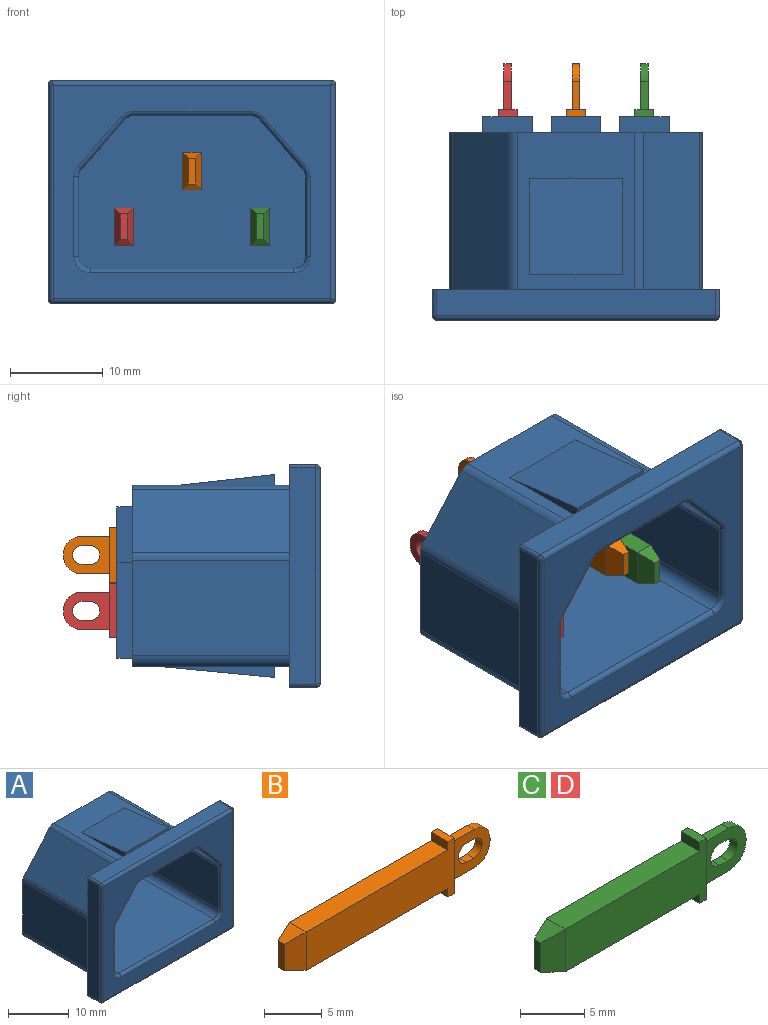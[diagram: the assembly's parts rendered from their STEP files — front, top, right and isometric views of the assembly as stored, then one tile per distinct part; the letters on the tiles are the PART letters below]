
ASSEMBLY  parts=4 mates=3
PART A: 98 faces, bbox 30.9x21.9x24.1 mm
  f0: plane 27.18x19.58mm, normal (0,1,0), area 315.8mm2, adj f45,f46,f47,f48,f49,f50,f52,f53
  f1: plane 12.05x1.14mm, normal (1,0,0), area 6.9mm2, adj f48,f62,f67
  f2: plane 10.31x1.14mm, normal (-1,0,0), area 5.9mm2, adj f45,f59,f60
  f3: plane 18.67x5.33mm, normal (0.75,0,-0.66), area 132.2mm2, adj f19,f24,f35,f51
  f4: plane 18.67x12.56mm, normal (0,0,-1), area 234.6mm2, adj f19,f20,f31,f51
  f5: plane 18.67x5.33mm, normal (-0.75,0,-0.66), area 132.2mm2, adj f20,f21,f27,f51
  f6: plane 18.67x8.57mm, normal (-1,0,0), area 159.9mm2, adj f21,f22,f26,f51
  f7: plane 21.89x18.67mm, normal (0,0,1), area 408.8mm2, adj f22,f23,f30,f51
  f8: plane 23.29x2.79mm, normal (-1,0,0), area 65.1mm2, adj f14,f15,f18,f42
  f9: plane 30.18x2.79mm, normal (0,0,-1), area 84.3mm2, adj f14,f15,f16,f43
  f10: plane 23.29x2.79mm, normal (1,0,0), area 65.1mm2, adj f14,f16,f17,f39
  f11: plane 30.18x2.79mm, normal (0,0,1), area 84.3mm2, adj f14,f17,f18,f38
  f12: plane 18.67x8.57mm, normal (1,0,0), area 159.9mm2, adj f23,f24,f34,f51
  f13: plane 29.92x23.04mm, normal (0,-1,0), area 283.1mm2, adj f25,f26,f27,f28,f29,f30,f31,f32
  f14: plane 30.94x24.05mm, normal (0,1,0), area 263.3mm2, adj f8,f9,f10,f11,f15,f16,f17,f18
  f15: cylinder r=0.38mm len=2.79mm, axis (0,-1,0), area 1.7mm2, adj f8,f9,f14,f44
  f16: cylinder r=0.38mm len=2.79mm, axis (0,1,0), area 1.7mm2, adj f9,f10,f14,f41
  f17: cylinder r=0.38mm len=2.79mm, axis (0,-1,0), area 1.7mm2, adj f10,f11,f14,f37
  f18: cylinder r=0.38mm len=2.79mm, axis (0,1,0), area 1.7mm2, adj f8,f11,f14,f40
  f19: cylinder r=1.27mm len=18.67mm, axis (0,-1,0), area 20.2mm2, adj f3,f4,f33,f51
  f20: cylinder r=1.27mm len=18.67mm, axis (0,-1,0), area 20.2mm2, adj f4,f5,f29,f51
  f21: cylinder r=1.27mm len=18.67mm, axis (0,-1,0), area 17.1mm2, adj f5,f6,f25,f51
  f22: cylinder r=1.27mm len=18.67mm, axis (0,-1,0), area 37.2mm2, adj f6,f7,f28,f51
  f23: cylinder r=1.27mm len=18.67mm, axis (0,-1,0), area 37.2mm2, adj f7,f12,f32,f51
  f24: cylinder r=1.27mm len=18.67mm, axis (0,-1,0), area 17.1mm2, adj f3,f12,f36,f51
  f25: torus R=1.78mm, axis (0,-1,0), area 0.8mm2, adj f13,f21,f26,f27
  f26: cylinder r=0.51mm len=8.57mm, axis (0,0,1), area 6.8mm2, adj f6,f13,f25,f28
  f27: cylinder r=0.51mm len=5.66mm, axis (-0.66,0,0.75), area 5.7mm2, adj f5,f13,f25,f29
  f28: torus R=1.78mm, axis (0,-1,0), area 1.8mm2, adj f13,f22,f26,f30
  f29: torus R=1.78mm, axis (0,-1,0), area 1mm2, adj f13,f20,f27,f31
  f30: cylinder r=0.51mm len=21.89mm, axis (1,0,0), area 17.5mm2, adj f7,f13,f28,f32
  f31: cylinder r=0.51mm len=12.56mm, axis (-1,0,0), area 10mm2, adj f4,f13,f29,f33
  f32: torus R=1.78mm, axis (0,-1,0), area 1.8mm2, adj f13,f23,f30,f34
  f33: torus R=1.78mm, axis (0,-1,0), area 1mm2, adj f13,f19,f31,f35
  f34: cylinder r=0.51mm len=8.57mm, axis (0,0,-1), area 6.8mm2, adj f12,f13,f32,f36
  f35: cylinder r=0.51mm len=5.66mm, axis (-0.66,0,-0.75), area 5.7mm2, adj f3,f13,f33,f36
  f36: torus R=1.78mm, axis (0,-1,0), area 0.8mm2, adj f13,f24,f34,f35
  f37: bspline ~0.62x0.51mm, area 0.3mm2, adj f17,f38,f39
  f38: cylinder r=0.51mm len=30.18mm, axis (1,0,0), area 24mm2, adj f11,f13,f37,f40
  f39: cylinder r=0.51mm len=23.29mm, axis (0,0,-1), area 18.5mm2, adj f10,f13,f37,f41
  f40: bspline ~0.62x0.51mm, area 0.3mm2, adj f18,f38,f42
  f41: bspline ~0.62x0.51mm, area 0.3mm2, adj f16,f39,f43
  f42: cylinder r=0.51mm len=23.29mm, axis (0,0,1), area 18.5mm2, adj f8,f13,f40,f44
  f43: cylinder r=0.51mm len=30.18mm, axis (-1,0,0), area 24mm2, adj f9,f13,f41,f44
  f44: bspline ~0.62x0.51mm, area 0.3mm2, adj f15,f42,f43
  f45: plane 16.97x12.71mm, normal (0,0,1), area 112.7mm2, adj f0,f2,f14,f52,f57,f58,f59,f60
  f46: plane 16.97x6.81mm, normal (0.75,0,0.66), area 153.6mm2, adj f0,f14,f52,f53
  f47: plane 16.97x10.23mm, normal (1,0,0), area 173.6mm2, adj f0,f14,f53,f54
  f48: plane 24.64x16.97mm, normal (0,0,-1), area 307.9mm2, adj f0,f1,f14,f54,f55,f61,f62,f63
  f49: plane 16.97x10.23mm, normal (-1,0,0), area 173.6mm2, adj f0,f14,f55,f56
  f50: plane 16.97x6.81mm, normal (-0.75,0,0.66), area 153.6mm2, adj f0,f14,f56,f57
  f51: plane 24.44x16.43mm, normal (0,-1,0), area 367.9mm2, adj f3,f4,f5,f6,f7,f12,f19,f20
  f52: cylinder r=1.27mm len=16.97mm, axis (0,-1,0), area 18.4mm2, adj f0,f14,f45,f46
  f53: cylinder r=1.27mm len=16.97mm, axis (0,-1,0), area 15.5mm2, adj f0,f14,f46,f47
  f54: cylinder r=1.27mm len=16.97mm, axis (0,-1,0), area 33.8mm2, adj f0,f14,f47,f48
  f55: cylinder r=1.27mm len=16.97mm, axis (0,-1,0), area 33.8mm2, adj f0,f14,f48,f49
  f56: cylinder r=1.27mm len=16.97mm, axis (0,-1,0), area 15.5mm2, adj f0,f14,f49,f50
  f57: cylinder r=1.27mm len=16.97mm, axis (0,-1,0), area 18.4mm2, adj f0,f14,f45,f50
  f58: plane 10.31x1.14mm, normal (1,0,0), area 5.9mm2, adj f45,f59,f60
  f59: plane 9.98x1.14mm, normal (0,-1,0), area 11.4mm2, adj f2,f45,f58,f60
  f60: plane 10.31x9.98mm, normal (0,0.11,0.99), area 103.6mm2, adj f2,f45,f58,f59
  f61: plane 12.05x1.14mm, normal (-1,0,0), area 6.9mm2, adj f48,f62,f67
  f62: plane 4.57x1.14mm, normal (0,-1,0), area 5.2mm2, adj f1,f48,f61,f67
  f63: plane 12.05x1.14mm, normal (1,0,0), area 6.9mm2, adj f48,f64,f66
  f64: plane 4.57x1.14mm, normal (0,-1,0), area 5.2mm2, adj f48,f63,f65,f66
  f65: plane 12.05x1.14mm, normal (-1,0,0), area 6.9mm2, adj f48,f64,f66
  f66: plane 12.05x4.57mm, normal (0,0.09,-1), area 55.3mm2, adj f48,f63,f64,f65
  f67: plane 12.05x4.57mm, normal (0,0.09,-1), area 55.3mm2, adj f1,f48,f61,f62
  f68: plane 2.03x1.65mm, normal (0,0,-1), area 3.4mm2, adj f69,f75,f76,f77
  f69: plane 4.01x1.65mm, normal (1,0,0), area 6.6mm2, adj f68,f70,f76,f77
  f70: plane 2.03x1.65mm, normal (0,0,1), area 3.4mm2, adj f69,f75,f76,f77
  f71: plane 10.31x1.65mm, normal (-1,0,0), area 17mm2, adj f0,f72,f74,f76
  f72: plane 5.33x1.65mm, normal (0,0,1), area 8.8mm2, adj f0,f71,f73,f76
  f73: plane 10.31x1.65mm, normal (1,0,0), area 17mm2, adj f0,f72,f74,f76
  f74: plane 5.33x1.65mm, normal (0,0,-1), area 8.8mm2, adj f0,f71,f73,f76
  f75: plane 4.01x1.65mm, normal (-1,0,0), area 6.6mm2, adj f68,f70,f76,f77
  f76: plane 10.31x5.33mm, normal (0,1,0), area 46.9mm2, adj f68,f69,f70,f71,f72,f73,f74,f75
  f77: plane 4.01x2.03mm, normal (0,1,0), area 8.2mm2, adj f68,f69,f70,f75
  f78: plane 2.03x1.65mm, normal (0,0,-1), area 3.4mm2, adj f79,f85,f86,f87
  f79: plane 4.01x1.65mm, normal (1,0,0), area 6.6mm2, adj f78,f80,f86,f87
  f80: plane 2.03x1.65mm, normal (0,0,1), area 3.4mm2, adj f79,f85,f86,f87
  f81: plane 10.31x1.65mm, normal (-1,0,0), area 17mm2, adj f0,f82,f84,f86
  f82: plane 5.33x1.65mm, normal (0,0,1), area 8.8mm2, adj f0,f81,f83,f86
  f83: plane 10.31x1.65mm, normal (1,0,0), area 17mm2, adj f0,f82,f84,f86
  f84: plane 5.33x1.65mm, normal (0,0,-1), area 8.8mm2, adj f0,f81,f83,f86
  f85: plane 4.01x1.65mm, normal (-1,0,0), area 6.6mm2, adj f78,f80,f86,f87
  f86: plane 10.31x5.33mm, normal (0,1,0), area 46.9mm2, adj f78,f79,f80,f81,f82,f83,f84,f85
  f87: plane 4.01x2.03mm, normal (0,1,0), area 8.2mm2, adj f78,f79,f80,f85
  f88: plane 2.03x1.65mm, normal (0,0,-1), area 3.4mm2, adj f89,f95,f96,f97
  f89: plane 4.01x1.65mm, normal (1,0,0), area 6.6mm2, adj f88,f90,f96,f97
  f90: plane 2.03x1.65mm, normal (0,0,1), area 3.4mm2, adj f89,f95,f96,f97
  f91: plane 10.31x1.65mm, normal (-1,0,0), area 17mm2, adj f0,f92,f94,f96
  f92: plane 5.33x1.65mm, normal (0,0,1), area 8.8mm2, adj f0,f91,f93,f96
  f93: plane 10.31x1.65mm, normal (1,0,0), area 17mm2, adj f0,f92,f94,f96
  f94: plane 5.33x1.65mm, normal (0,0,-1), area 8.8mm2, adj f0,f91,f93,f96
  f95: plane 4.01x1.65mm, normal (-1,0,0), area 6.6mm2, adj f88,f90,f96,f97
  f96: plane 10.31x5.33mm, normal (0,1,0), area 46.9mm2, adj f88,f89,f90,f91,f92,f93,f94,f95
  f97: plane 4.01x2.03mm, normal (0,1,0), area 8.2mm2, adj f88,f89,f90,f95
PART B: 25 faces, bbox 25.1x2x5.8 mm
  f0: plane 3.07x0.84mm, normal (0,0,-1), area 2.6mm2, adj f1,f10,f15,f16
  f1: cylinder r=1.91mm len=1.91mm, axis (0,1,0), area 2.5mm2, adj f0,f2,f15,f16
  f2: plane 0.84x0.25mm, normal (1,0,0), area 0.2mm2, adj f1,f3,f15,f16
  f3: cylinder r=1.91mm len=1.91mm, axis (0,1,0), area 2.5mm2, adj f2,f4,f15,f16
  f4: plane 3.07x0.84mm, normal (0,0,1), area 2.6mm2, adj f3,f10,f15,f16
  f5: plane 17.35x2.03mm, normal (0,0,1), area 35.3mm2, adj f12,f13,f14,f22
  f6: plane 2.79x0.76mm, normal (-1,0,0), area 2.1mm2, adj f21,f22,f23,f24
  f7: plane 17.35x2.03mm, normal (0,0,-1), area 35.3mm2, adj f8,f13,f14,f23
  f8: plane 2.03x0.89mm, normal (-1,0,0), area 1.8mm2, adj f7,f9,f13,f14
  f9: plane 2.03x0.76mm, normal (0,0,-1), area 1.5mm2, adj f8,f10,f13,f14
  f10: plane 5.84x2.03mm, normal (1,0,0), area 8.5mm2, adj f0,f4,f9,f11,f13,f14,f15,f16
  f11: plane 2.03x0.76mm, normal (0,0,1), area 1.5mm2, adj f10,f12,f13,f14
  f12: plane 2.03x0.89mm, normal (-1,0,0), area 1.8mm2, adj f5,f11,f13,f14
  f13: plane 18.11x5.84mm, normal (0,-1,0), area 75mm2, adj f5,f7,f8,f9,f10,f11,f12,f24
  f14: plane 18.11x5.84mm, normal (0,1,0), area 75mm2, adj f5,f7,f8,f9,f10,f11,f12,f21
  f15: plane 4.98x4.06mm, normal (0,1,0), area 13.6mm2, adj f0,f1,f2,f3,f4,f10,f17,f18
  f16: plane 4.98x4.06mm, normal (0,-1,0), area 13.6mm2, adj f0,f1,f2,f3,f4,f10,f17,f18
  f17: plane 0.89x0.84mm, normal (0,0,1), area 0.7mm2, adj f15,f16,f18,f20
  f18: cylinder r=1.02mm len=2.03mm, axis (0,1,0), area 2.7mm2, adj f15,f16,f17,f19
  f19: plane 0.89x0.84mm, normal (0,0,-1), area 0.7mm2, adj f15,f16,f18,f20
  f20: cylinder r=1.02mm len=2.03mm, axis (0,1,0), area 2.7mm2, adj f15,f16,f17,f19
  f21: plane 4.06x2.03mm, normal (-0.3,0.95,0), area 7.3mm2, adj f6,f14,f22,f23
  f22: plane 2.03x2.03mm, normal (-0.3,0,0.95), area 3mm2, adj f5,f6,f21,f24
  f23: plane 2.03x2.03mm, normal (-0.3,0,-0.95), area 3mm2, adj f6,f7,f21,f24
  f24: plane 4.06x2.03mm, normal (-0.3,-0.95,0), area 7.3mm2, adj f6,f13,f22,f23
PART C: 25 faces, bbox 22.6x2x5.8 mm
  f0: plane 3.07x0.81mm, normal (0,0,-1), area 2.5mm2, adj f1,f10,f15,f16
  f1: cylinder r=1.91mm len=1.91mm, axis (0,1,0), area 2.4mm2, adj f0,f2,f15,f16
  f2: plane 0.81x0.25mm, normal (1,0,0), area 0.2mm2, adj f1,f3,f15,f16
  f3: cylinder r=1.91mm len=1.91mm, axis (0,1,0), area 2.4mm2, adj f2,f4,f15,f16
  f4: plane 3.07x0.81mm, normal (0,0,1), area 2.5mm2, adj f3,f10,f15,f16
  f5: plane 14.81x2.03mm, normal (0,0,1), area 30.1mm2, adj f12,f13,f14,f22
  f6: plane 2.79x0.76mm, normal (-1,0,0), area 2.1mm2, adj f21,f22,f23,f24
  f7: plane 14.81x2.03mm, normal (0,0,-1), area 30.1mm2, adj f8,f13,f14,f23
  f8: plane 2.03x0.89mm, normal (-1,0,0), area 1.8mm2, adj f7,f9,f13,f14
  f9: plane 2.03x0.76mm, normal (0,0,-1), area 1.5mm2, adj f8,f10,f13,f14
  f10: plane 5.84x2.03mm, normal (1,0,0), area 8.6mm2, adj f0,f4,f9,f11,f13,f14,f15,f16
  f11: plane 2.03x0.76mm, normal (0,0,1), area 1.5mm2, adj f10,f12,f13,f14
  f12: plane 2.03x0.89mm, normal (-1,0,0), area 1.8mm2, adj f5,f11,f13,f14
  f13: plane 15.57x5.84mm, normal (0,-1,0), area 64.6mm2, adj f5,f7,f8,f9,f10,f11,f12,f24
  f14: plane 15.57x5.84mm, normal (0,1,0), area 64.6mm2, adj f5,f7,f8,f9,f10,f11,f12,f21
  f15: plane 4.98x4.06mm, normal (0,1,0), area 13.6mm2, adj f0,f1,f2,f3,f4,f10,f17,f18
  f16: plane 4.98x4.06mm, normal (0,-1,0), area 13.6mm2, adj f0,f1,f2,f3,f4,f10,f17,f18
  f17: plane 0.89x0.81mm, normal (0,0,1), area 0.7mm2, adj f15,f16,f18,f20
  f18: cylinder r=1.02mm len=2.03mm, axis (0,1,0), area 2.6mm2, adj f15,f16,f17,f19
  f19: plane 0.89x0.81mm, normal (0,0,-1), area 0.7mm2, adj f15,f16,f18,f20
  f20: cylinder r=1.02mm len=2.03mm, axis (0,1,0), area 2.6mm2, adj f15,f16,f17,f19
  f21: plane 4.06x2.03mm, normal (-0.3,0.95,0), area 7.3mm2, adj f6,f14,f22,f23
  f22: plane 2.03x2.03mm, normal (-0.3,0,0.95), area 3mm2, adj f5,f6,f21,f24
  f23: plane 2.03x2.03mm, normal (-0.3,0,-0.95), area 3mm2, adj f6,f7,f21,f24
  f24: plane 4.06x2.03mm, normal (-0.3,-0.95,0), area 7.3mm2, adj f6,f13,f22,f23
PART D: same geometry as C
PLACE A t=(6.41,-4.91,18.4)mm
PLACE B rot(axis=(0,0,1),90deg) t=(-29.58,-11.35,31.74)mm
PLACE C rot(axis=(0,0,1),90deg) t=(-22.21,-5.27,3.32)mm
PLACE D rot(axis=(0,0,1),90deg) t=(-36.95,-5.27,3.32)mm
MATE fastened C.f12 <-> A.f76  axis (0,-1,0) through (-17.9,13.71,2.28)mm
MATE fastened B.f12 <-> A.f96  axis (0,-1,0) through (-25.26,13.71,8.29)mm
MATE fastened D.f12 <-> A.f86  axis (0,-1,0) through (-32.63,13.71,2.28)mm
